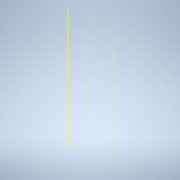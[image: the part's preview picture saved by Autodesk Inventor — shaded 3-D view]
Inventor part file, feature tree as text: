
AUTODESK INVENTOR PART (.ipt)
format: ipt  version: 2021 (Build 250183000, 183)  size: 240,640 bytes
history: native  units: in
note: dims shown in document units (in); Inventor stores cm internally (conversion verified against a paired STEP export)
features: reference x8, other x7, sketch x6, fillet x5, extrude x4, plane x2, projected_geometry x2, hole x1
ambient origin geometry x8: Origin, YZ Plane, XZ Plane, XY Plane, X Axis, Y Axis, Z Axis, Center Point
bodies: Body1 (feature_tree)
feature tree (35):
  other  "Work Axis2"
  extrude  "Extrusion3"  Depth=0.1181in
  extrude  "Extrusion4"  Depth=0.1969in
  hole  "Hole1"  [1 undecoded]
  extrude  "Extrusion5"  Depth=0.1181in
  plane  "Work Plane1"
  other  "Work Axis3"
  other  "Work Axis4"
  plane  "Work Plane2"
  sketch  "Sketch7"  dims[d20=0.3937in d21=0.0in]
  extrude  "Extrusion6"  Depth=0.1969in
  fillet  "Fillet1"  Radius=0.1378in
  fillet  "Fillet2"  Radius=0.0079in
  fillet  "Fillet3"  Radius=0.0472in
  fillet  "Fillet4"  Radius=0.0157in
  fillet  "Fillet5"  Radius=0.0787in
  sketch  "Sketch3"  dims[d11=0.1181in d12=0.1181in]
  reference  "Reference12"
  reference  "Reference13"
  reference  "Reference14"
  reference  "Reference15"
  reference  "Reference16"
  sketch  "Sketch4"  dims[d13=0.1575in d14=0.1969in]
  sketch  "Sketch5"  dims[d15=0.3937in d16=0.0in d17=0.7874in]
  reference  "Reference17"
  reference  "Reference18"
  sketch  "Sketch6"  dims[d18=0.1181in d19=0.1181in]
  projected_geometry  "Projected Loop1"
  projected_geometry  "Projected Loop2"
  sketch  "Sketch8"  dims[d22=0.1181in d23=0.2362in d24=0.1575in d25=0.0787in d26=90.0deg d27=0.315in d28=0.8108in d29=0.1969in d30=0.1378in d31=0.0in d32=0.0079in d33=0.0472in d34=0.0157in d35=0.0787in d36=0.0315in d37=0.2362in d38=0.0in d39=0.0276in d40=0.3543in d41=0.3543in d42=0.1969in d43=0.1575in d44=0.1181in d45=0.0787in d5=0.0197in d6=0.0344in d7=0.0197in d8=0.0344in]
  reference  "Reference19"
  other  "assy_gic_kinematic_2d_robot_arm_MK1_v2.iam"
  other  "sub_assy_robot_arm_link1:1"
  other  "arm_1_v2:1"
  other  "Pololu 1-2in Ball caster:1"
note: 1 required parameter value undecoded (feature->parameter linkage not recoverable at this tier; creation-order binding heuristic only, values carry confidence <= 0.55)
